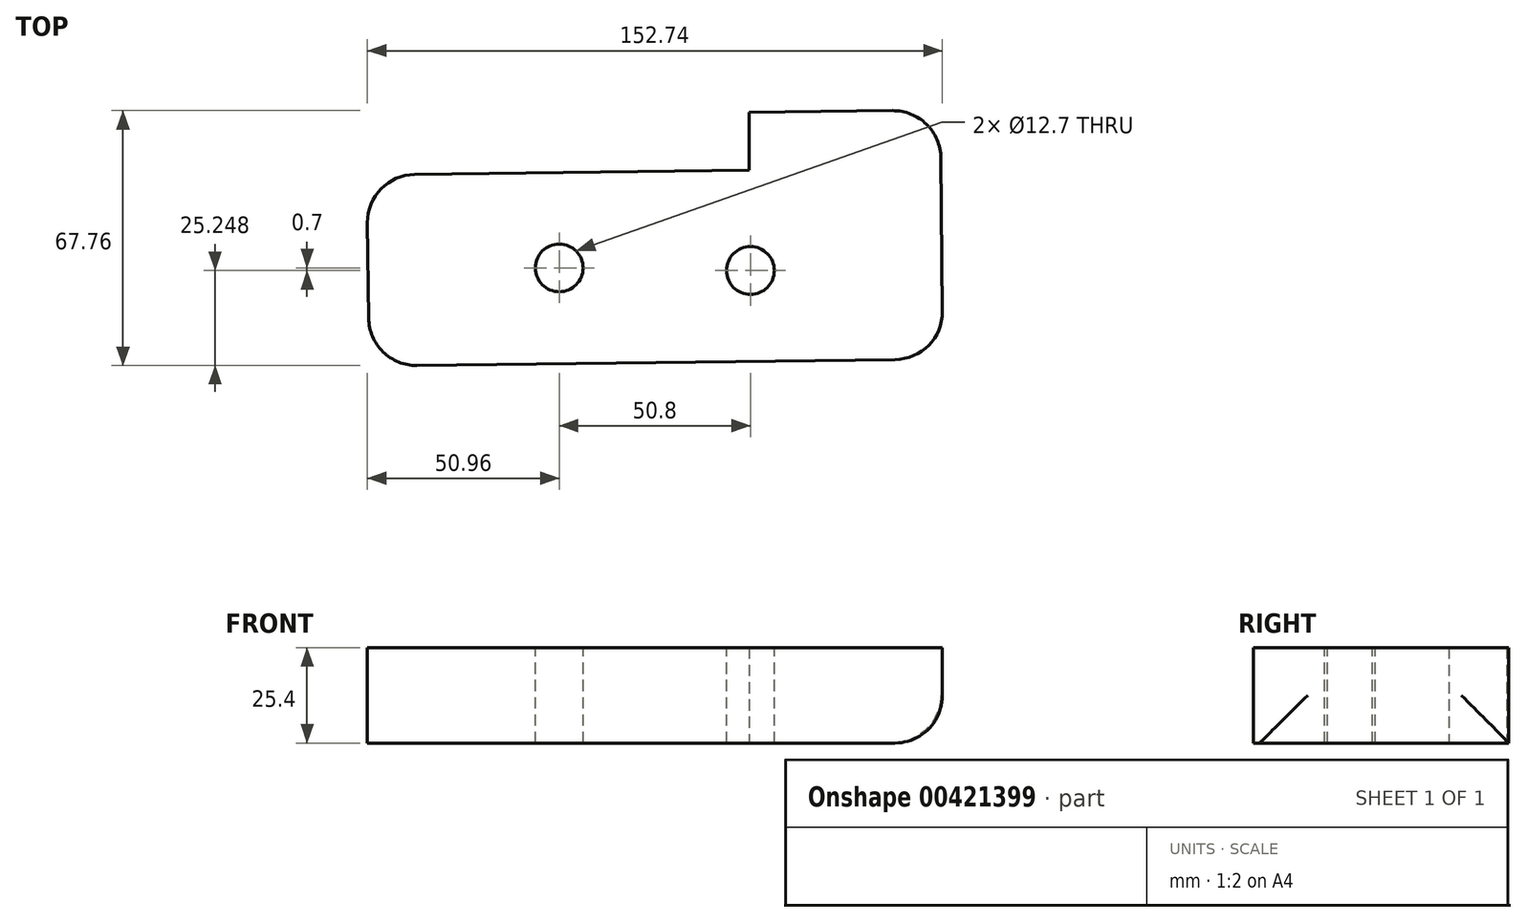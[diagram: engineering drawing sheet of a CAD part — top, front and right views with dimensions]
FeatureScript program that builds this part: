
annotation { "Feature Type Name" : "Feature", "Feature Type Description" : "" }
export const myFeature = defineFeature(function(context is Context, id is Id, definition is map)
    precondition{}
    {
        {
            var Q0;
            Q0=qCreatedBy(makeId("Top.planeOp"),FACE);
            var sketch = newSketch(context, id + "F0", { "sketchPlane" : qUnion([Q0])});
            skLineSegment(sketch, "E0", {"start": v(0, 0) * mm, "end": v(152.39, 1.86) * mm});
            skLineSegment(sketch, "E1", {"start": v(0, 0) * mm, "end": v(-0.62, 50.8) * mm});
            skLineSegment(sketch, "E2", {"start": v(-0.62, 50.8) * mm, "end": v(100.97, 52.04) * mm});
            skLineSegment(sketch, "E3", {"start": v(100.97, 52.04) * mm, "end": v(100.97, 67.45) * mm});
            skLineSegment(sketch, "E4", {"start": v(100.97, 67.45) * mm, "end": v(151.77, 68.07) * mm});
            skLineSegment(sketch, "E5", {"start": v(151.77, 68.07) * mm, "end": v(152.39, 1.86) * mm});
            skSolve(sketch);
        }
        {
            var Q0;
            Q0=makeQuery(id+"F0.imprint","IMPRINT",FACE,{"disambiguationData":[TD([[makeQuery(id+"F0.imprint","IMPRINT",EDGE,{"derivedFrom":sQuery(id+"F0.wireOp",EDGE,"E0")}),1.0]])]});
            extrude(context, id + "F1", {"entities" : qUnion([Q0]), "depth" : 25.4 * mm});
        }
        {
            var Q0;
            Q0=makeQuery(id+"F1.opExtrude","SWEPT_EDGE",EDGE,{"disambiguationData":[OSD([sQuery(id+"F0.wireOp",EDGE,"E1"),sQuery(id+"F0.wireOp",EDGE,"E2")])]});
            var Q1;
            Q1=makeQuery(id+"F1.opExtrude","CAP_EDGE",EDGE,{"disambiguationData":[OSD([sQuery(id+"F0.wireOp",EDGE,"E5")])],"isStart":true});
            var Q2;
            Q2=makeQuery(id+"F1.opExtrude","SWEPT_EDGE",EDGE,{"disambiguationData":[OSD([sQuery(id+"F0.wireOp",EDGE,"E0"),sQuery(id+"F0.wireOp",EDGE,"E5")])]});
            var Q3;
            Q3=makeQuery(id+"F1.opExtrude","SWEPT_EDGE",EDGE,{"disambiguationData":[OSD([sQuery(id+"F0.wireOp",EDGE,"E0"),sQuery(id+"F0.wireOp",EDGE,"E1")])]});
            var Q4;
            Q4=makeQuery(id+"F1.opExtrude","SWEPT_EDGE",EDGE,{"disambiguationData":[OSD([sQuery(id+"F0.wireOp",EDGE,"E4"),sQuery(id+"F0.wireOp",EDGE,"E5")])]});
            fillet(context, id + "F2", {"entities" : qUnion([Q0, Q1, Q2, Q3, Q4]), "radius" : 12.7 * mm, "tangentPropagation" : true, "allowEdgeOverflow" : false});
        }
        {
            var Q0;
            Q0=makeQuery(id+"F1.opExtrude","CAP_FACE",FACE,{"disambiguationData":[OSD([sQuery(id+"F0.wireOp",EDGE,"E0"),sQuery(id+"F0.wireOp",EDGE,"E1"),sQuery(id+"F0.wireOp",EDGE,"E2"),sQuery(id+"F0.wireOp",EDGE,"E3"),sQuery(id+"F0.wireOp",EDGE,"E4"),sQuery(id+"F0.wireOp",EDGE,"E5")])],"isStart":false});
            var sketch = newSketch(context, id + "F3", { "sketchPlane" : qUnion([Q0])});
            skPoint(sketch, "E6", {"position": v(-0.31, 25.4) * mm});
            skPoint(sketch, "E7", {"position": v(50.49, 26.1) * mm});
            skPoint(sketch, "E8", {"position": v(101.29, 25.4) * mm});
            skSolve(sketch);
        }
        {
            var Q0;
            Q0=sQuery(id+"F3.wireOp",VERTEX,"E8");
            var Q1;
            Q1=sQuery(id+"F3.wireOp",VERTEX,"E7");
            var Q2;
            Q2=makeQuery(id+"F1.opExtrude","SWEPT_BODY",BODY,{"disambiguationData":[OSD([sQuery(id+"F0.wireOp",EDGE,"E0"),sQuery(id+"F0.wireOp",EDGE,"E1"),sQuery(id+"F0.wireOp",EDGE,"E2"),sQuery(id+"F0.wireOp",EDGE,"E3"),sQuery(id+"F0.wireOp",EDGE,"E4"),sQuery(id+"F0.wireOp",EDGE,"E5")])]});
            hole(context, id + "F4", {"style" : HoleStyle.SIMPLE, "endStyle" : HoleEndStyle.THROUGH, "holeDiameter" : 12.7 * mm, "isTappedThrough" : true, "tappedDepth" : 12.7 * mm, "tapClearance" : 3, "locations" : qUnion([Q0, Q1]), "scope" : qUnion([Q2])});
        }
    });
